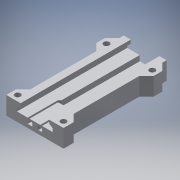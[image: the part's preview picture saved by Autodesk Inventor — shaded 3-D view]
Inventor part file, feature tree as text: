
AUTODESK INVENTOR PART (.ipt)
format: ipt  version: 2019 (Build 230136000, 136)  size: 248,832 bytes
history: native  units: in
note: dims shown in document units (in); Inventor stores cm internally (conversion verified against a paired STEP export)
features: extrude x6, sketch x5, projected_geometry x2, plane x1, chamfer x1, hole x1, mirror x1
ambient origin geometry x8: Origin, YZ Plane, XZ Plane, XY Plane, X Axis, Y Axis, Z Axis, Center Point
bodies: Solid1 (feature_tree)
feature tree (17):
  extrude  "Extrusion1"  Depth=2.0in
  plane  "Work Plane1"
  sketch  "Sketch2"  dims[d2=0.625in d3=0.0in d9=0.25in d10=0.0in]
  extrude  "Extrusion2"  Depth=0.25in TaperAngle=0.0deg
  extrude  "Extrusion3"  Depth=0.25in
  extrude  "Extrusion6"  Depth=0.25in
  chamfer  "Chamfer2"  Distance=0.125in
  sketch  "Sketch8"  dims[d21=0.4in d22=0.25in]
  hole  "Hole2"  [1 undecoded]
  extrude  "Extrusion7"  TaperAngle=30.0deg  [1 undecoded]
  mirror  "Mirror1"
  extrude  "Extrusion8"  Depth=0.125in
  sketch  "Sketch1"  dims[d0=2.0in d1=4.5in]
  projected_geometry  "Projected Loop1"
  sketch  "Sketch7"  dims[d11=-1.0in d20=0.25in]
  projected_geometry  "Projected Loop5"
  sketch  "Sketch9"  dims[d23=0.1875in d24=0.125in d25=0.125in d26=30.0deg d27=0.125in d28=0.125in d29=0.04in d30=0.25in d31=0.0in d45=0.0625in d46=0.125in d48=0.125in d50=30.0deg d63=135.0deg d64=0.0625in d65=0.05in d66=1.0in d67=0.0in d68=0.03in d69=0.125in d70=45.0deg d71=0.2031in d72=1.2in d73=0.2in d75=135.0deg d76=135.0deg d77=0.125in d80=0.203in d81=0.75in d82=0.375in d83=0.25in d84=0.5635in d85=1.0in d86=0.8108in d87=1.0in d88=0.0in d89=1.35in d91=0.2in d92=0.35in d93=0.65in d94=1.0in d95=0.0in]
note: 2 required parameter values undecoded (feature->parameter linkage not recoverable at this tier; creation-order binding heuristic only, values carry confidence <= 0.55)
